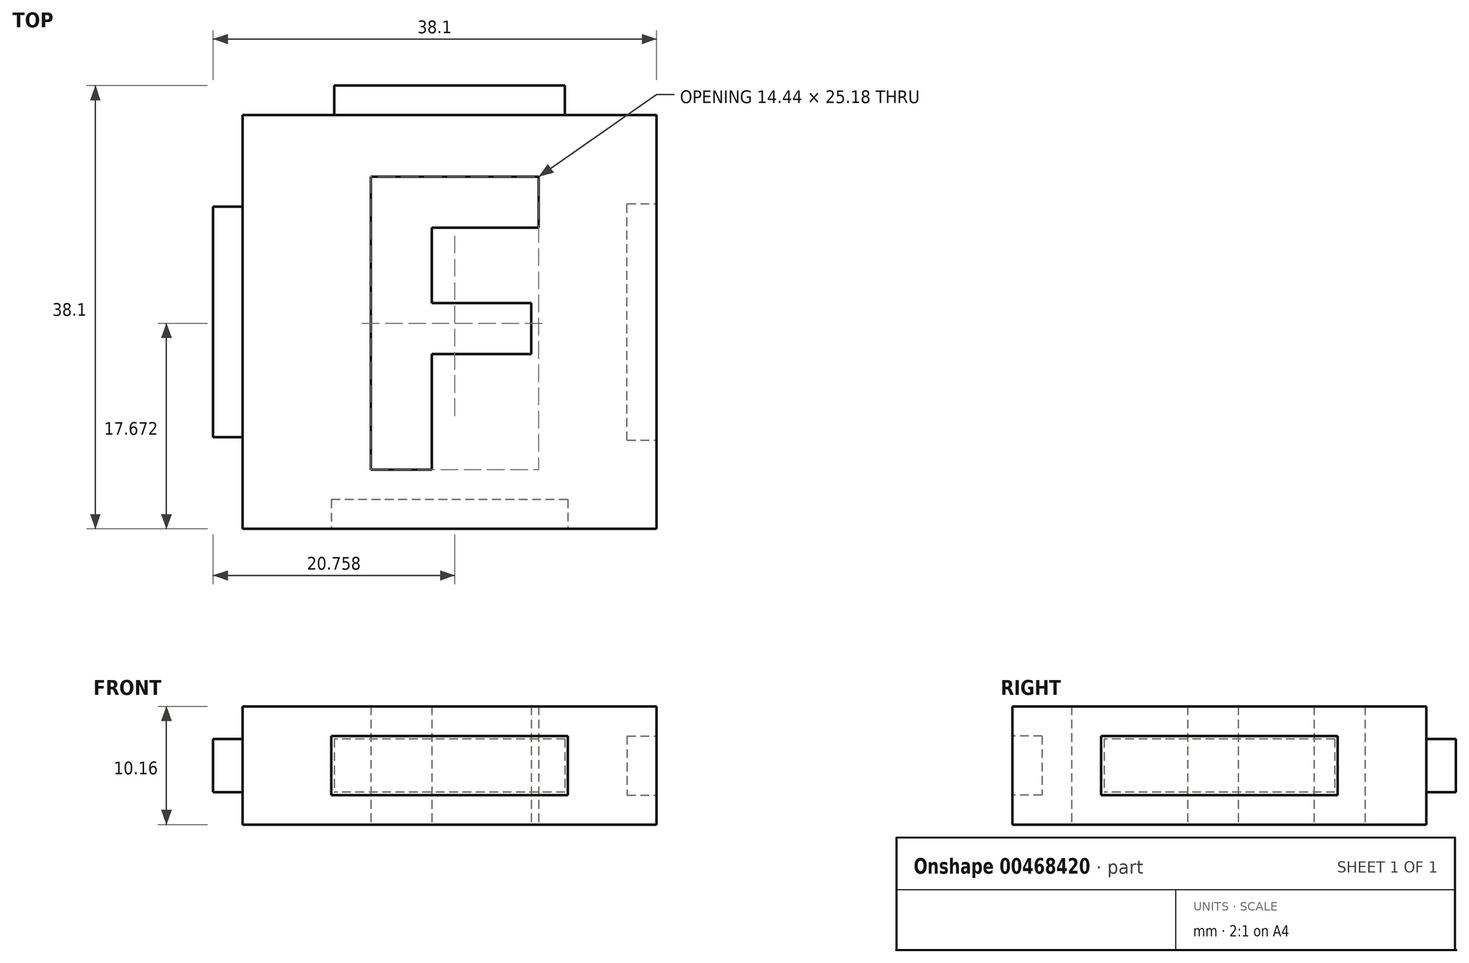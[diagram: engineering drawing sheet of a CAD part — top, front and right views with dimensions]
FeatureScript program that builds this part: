
annotation { "Feature Type Name" : "Feature", "Feature Type Description" : "" }
export const myFeature = defineFeature(function(context is Context, id is Id, definition is map)
    precondition{}
    {
        {
            var Q0;
            Q0=qCreatedBy(makeId("Top.planeOp"),FACE);
            var sketch = newSketch(context, id + "F0", { "sketchPlane" : qUnion([Q0])});
            skLineSegment(sketch, "E0.bottom", {"start": v(-17.78, 17.78) * mm, "end": v(17.78, 17.78) * mm});
            skLineSegment(sketch, "E0.top", {"start": v(-17.78, -17.78) * mm, "end": v(17.78, -17.78) * mm});
            skLineSegment(sketch, "E0.left", {"start": v(-17.78, 17.78) * mm, "end": v(-17.78, -17.78) * mm});
            skLineSegment(sketch, "E0.right", {"start": v(17.78, 17.78) * mm, "end": v(17.78, -17.78) * mm});
            skText(sketch, "E1", { "text": "F", "fontName": "OpenSans-Bold.ttf"});
            const initialGuessF0  = {"E1": [-0.00995, -0.0127, 1, 0, 0.0254]};
            skSetInitialGuess(sketch, initialGuessF0);
            skSolve(sketch);
        }
        {
            var Q0;
            Q0=qSketchRegion(id+"F0",true);
            extrude(context, id + "F1", {"entities" : qUnion([Q0]), "endBound" : BoundingType.SYMMETRIC, "depth" : 10.16 * mm});
        }
        {
            var Q0;
            Q0=makeQuery(id+"F1.opExtrude","SWEPT_FACE",FACE,{"disambiguationData":[OSD([sQuery(id+"F0.wireOp",EDGE,"E0.bottom")])]});
            var sketch = newSketch(context, id + "F2", { "sketchPlane" : qUnion([Q0])});
            skLineSegment(sketch, "E2.bottom", {"start": v(-9.9, 2.29) * mm, "end": v(9.9, 2.29) * mm});
            skLineSegment(sketch, "E2.top", {"start": v(-9.9, -2.29) * mm, "end": v(9.9, -2.29) * mm});
            skLineSegment(sketch, "E2.left", {"start": v(-9.9, 2.29) * mm, "end": v(-9.9, -2.29) * mm});
            skLineSegment(sketch, "E2.right", {"start": v(9.9, 2.29) * mm, "end": v(9.9, -2.29) * mm});
            skSolve(sketch);
        }
        {
            var Q0;
            Q0=qSketchRegion(id+"F2",true);
            extrude(context, id + "F3", {"entities" : qUnion([Q0]), "operationType" : NewBodyOperationType.ADD, "depth" : 2.54 * mm});
        }
        {
            var Q0;
            Q0=makeQuery(id+"F1.opExtrude","SWEPT_FACE",FACE,{"disambiguationData":[OSD([sQuery(id+"F0.wireOp",EDGE,"E0.left")])]});
            var sketch = newSketch(context, id + "F4", { "sketchPlane" : qUnion([Q0])});
            skLineSegment(sketch, "E3.bottom", {"start": v(-9.9, 2.29) * mm, "end": v(9.9, 2.29) * mm});
            skLineSegment(sketch, "E3.top", {"start": v(-9.9, -2.29) * mm, "end": v(9.9, -2.29) * mm});
            skLineSegment(sketch, "E3.left", {"start": v(-9.9, 2.29) * mm, "end": v(-9.9, -2.29) * mm});
            skLineSegment(sketch, "E3.right", {"start": v(9.9, 2.29) * mm, "end": v(9.9, -2.29) * mm});
            skSolve(sketch);
        }
        {
            var Q0;
            Q0=qSketchRegion(id+"F4",true);
            extrude(context, id + "F5", {"entities" : qUnion([Q0]), "operationType" : NewBodyOperationType.ADD, "depth" : 2.54 * mm});
        }
        {
            var Q0;
            Q0=makeQuery(id+"F1.opExtrude","SWEPT_FACE",FACE,{"disambiguationData":[OSD([sQuery(id+"F0.wireOp",EDGE,"E0.top")])]});
            var sketch = newSketch(context, id + "F6", { "sketchPlane" : qUnion([Q0])});
            skLineSegment(sketch, "E4.bottom", {"start": v(-10.16, 2.54) * mm, "end": v(10.16, 2.54) * mm});
            skLineSegment(sketch, "E4.top", {"start": v(-10.16, -2.54) * mm, "end": v(10.16, -2.54) * mm});
            skLineSegment(sketch, "E4.left", {"start": v(-10.16, 2.54) * mm, "end": v(-10.16, -2.54) * mm});
            skLineSegment(sketch, "E4.right", {"start": v(10.16, 2.54) * mm, "end": v(10.16, -2.54) * mm});
            skSolve(sketch);
        }
        {
            var Q0;
            Q0=qSketchRegion(id+"F6",true);
            extrude(context, id + "F7", {"entities" : qUnion([Q0]), "operationType" : NewBodyOperationType.REMOVE, "oppositeDirection" : true, "depth" : 2.54 * mm});
        }
        {
            var Q0;
            Q0=makeQuery(id+"F1.opExtrude","SWEPT_FACE",FACE,{"disambiguationData":[OSD([sQuery(id+"F0.wireOp",EDGE,"E0.right")])]});
            var sketch = newSketch(context, id + "F8", { "sketchPlane" : qUnion([Q0])});
            skLineSegment(sketch, "E5.bottom", {"start": v(-10.16, 2.54) * mm, "end": v(10.16, 2.54) * mm});
            skLineSegment(sketch, "E5.top", {"start": v(-10.16, -2.54) * mm, "end": v(10.16, -2.54) * mm});
            skLineSegment(sketch, "E5.left", {"start": v(-10.16, 2.54) * mm, "end": v(-10.16, -2.54) * mm});
            skLineSegment(sketch, "E5.right", {"start": v(10.16, 2.54) * mm, "end": v(10.16, -2.54) * mm});
            skSolve(sketch);
        }
        {
            var Q0;
            Q0=qSketchRegion(id+"F8",true);
            extrude(context, id + "F9", {"entities" : qUnion([Q0]), "operationType" : NewBodyOperationType.REMOVE, "oppositeDirection" : true, "depth" : 2.54 * mm});
        }
    });
